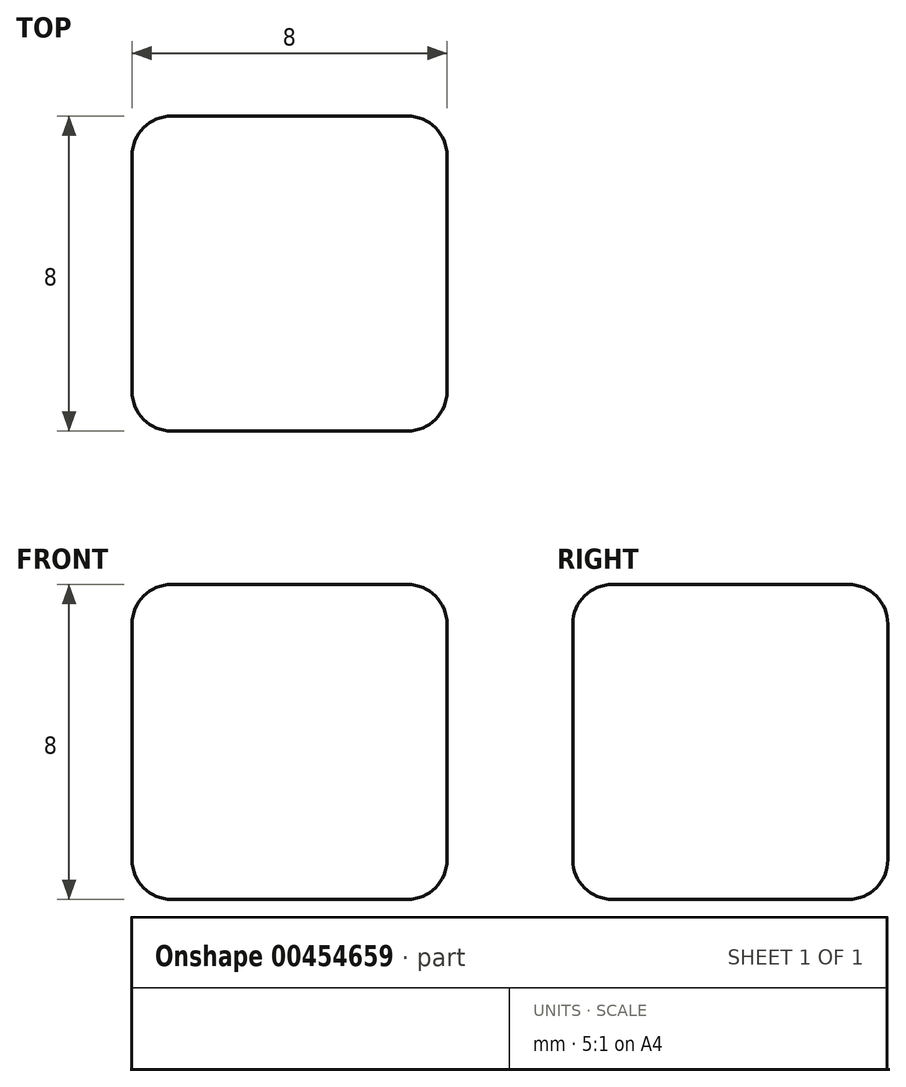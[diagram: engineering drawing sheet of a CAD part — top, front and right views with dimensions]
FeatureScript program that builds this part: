
annotation { "Feature Type Name" : "Feature", "Feature Type Description" : "" }
export const myFeature = defineFeature(function(context is Context, id is Id, definition is map)
    precondition{}
    {
        {
            var Q0;
            Q0=qCreatedBy(makeId("Top.planeOp"),FACE);
            var sketch = newSketch(context, id + "F0", { "sketchPlane" : qUnion([Q0])});
            skLineSegment(sketch, "E0.bottom", {"start": v(0, 0) * mm, "end": v(8, 0) * mm});
            skLineSegment(sketch, "E0.top", {"start": v(0, 8) * mm, "end": v(8, 8) * mm});
            skLineSegment(sketch, "E0.left", {"start": v(0, 0) * mm, "end": v(0, 8) * mm});
            skLineSegment(sketch, "E0.right", {"start": v(8, 0) * mm, "end": v(8, 8) * mm});
            skSolve(sketch);
        }
        {
            var Q0;
            Q0 = qSketchRegion(id + "F0", true);
            extrude(context, id + "F1", {"entities" : qUnion([Q0]), "depth" : 8 * mm, "offsetDistance" : 25 * mm});
        }
        {
            var Q0;
            Q0=makeQuery(id+"F1.opExtrude","CAP_EDGE",EDGE,{"disambiguationData":[OSD([sQuery(id+"F0.wireOp",EDGE,"E0.bottom")])],"isStart":false});
            var Q1;
            Q1=makeQuery(id+"F1.opExtrude","CAP_EDGE",EDGE,{"disambiguationData":[OSD([sQuery(id+"F0.wireOp",EDGE,"E0.top")])],"isStart":false});
            var Q2;
            Q2=makeQuery(id+"F1.opExtrude","CAP_EDGE",EDGE,{"disambiguationData":[OSD([sQuery(id+"F0.wireOp",EDGE,"E0.right")])],"isStart":false});
            var Q3;
            Q3=makeQuery(id+"F1.opExtrude","SWEPT_EDGE",EDGE,{"disambiguationData":[OSD([sQuery(id+"F0.wireOp",EDGE,"E0.bottom"),sQuery(id+"F0.wireOp",EDGE,"E0.right")])]});
            var Q4;
            Q4=makeQuery(id+"F1.opExtrude","SWEPT_EDGE",EDGE,{"disambiguationData":[OSD([sQuery(id+"F0.wireOp",EDGE,"E0.top"),sQuery(id+"F0.wireOp",EDGE,"E0.right")])]});
            var Q5;
            Q5=makeQuery(id+"F1.opExtrude","CAP_EDGE",EDGE,{"disambiguationData":[OSD([sQuery(id+"F0.wireOp",EDGE,"E0.right")])],"isStart":true});
            var Q6;
            Q6=makeQuery(id+"F1.opExtrude","SWEPT_EDGE",EDGE,{"disambiguationData":[OSD([sQuery(id+"F0.wireOp",EDGE,"E0.bottom"),sQuery(id+"F0.wireOp",EDGE,"E0.left")])]});
            var Q7;
            Q7=makeQuery(id+"F1.opExtrude","CAP_EDGE",EDGE,{"disambiguationData":[OSD([sQuery(id+"F0.wireOp",EDGE,"E0.left")])],"isStart":false});
            var Q8;
            Q8=makeQuery(id+"F1.opExtrude","SWEPT_FACE",FACE,{"disambiguationData":[OSD([sQuery(id+"F0.wireOp",EDGE,"E0.bottom")])]});
            var Q9;
            Q9=makeQuery(id+"F1.opExtrude","CAP_EDGE",EDGE,{"disambiguationData":[OSD([sQuery(id+"F0.wireOp",EDGE,"E0.left")])],"isStart":true});
            var Q10;
            Q10=makeQuery(id+"F1.opExtrude","SWEPT_EDGE",EDGE,{"disambiguationData":[OSD([sQuery(id+"F0.wireOp",EDGE,"E0.top"),sQuery(id+"F0.wireOp",EDGE,"E0.left")])]});
            var Q11;
            Q11=makeQuery(id+"F1.opExtrude","CAP_EDGE",EDGE,{"disambiguationData":[OSD([sQuery(id+"F0.wireOp",EDGE,"E0.top")])],"isStart":true});
            fillet(context, id + "F2", {"entities" : qUnion([Q0, Q1, Q2, Q3, Q4, Q5, Q6, Q7, Q8, Q9, Q10, Q11]), "tangentPropagation" : true, "radius" : 1 * mm, "defaultsChanged" : true, "vertexSettings" : [], "allowEdgeOverflow" : false});
        }
    });
